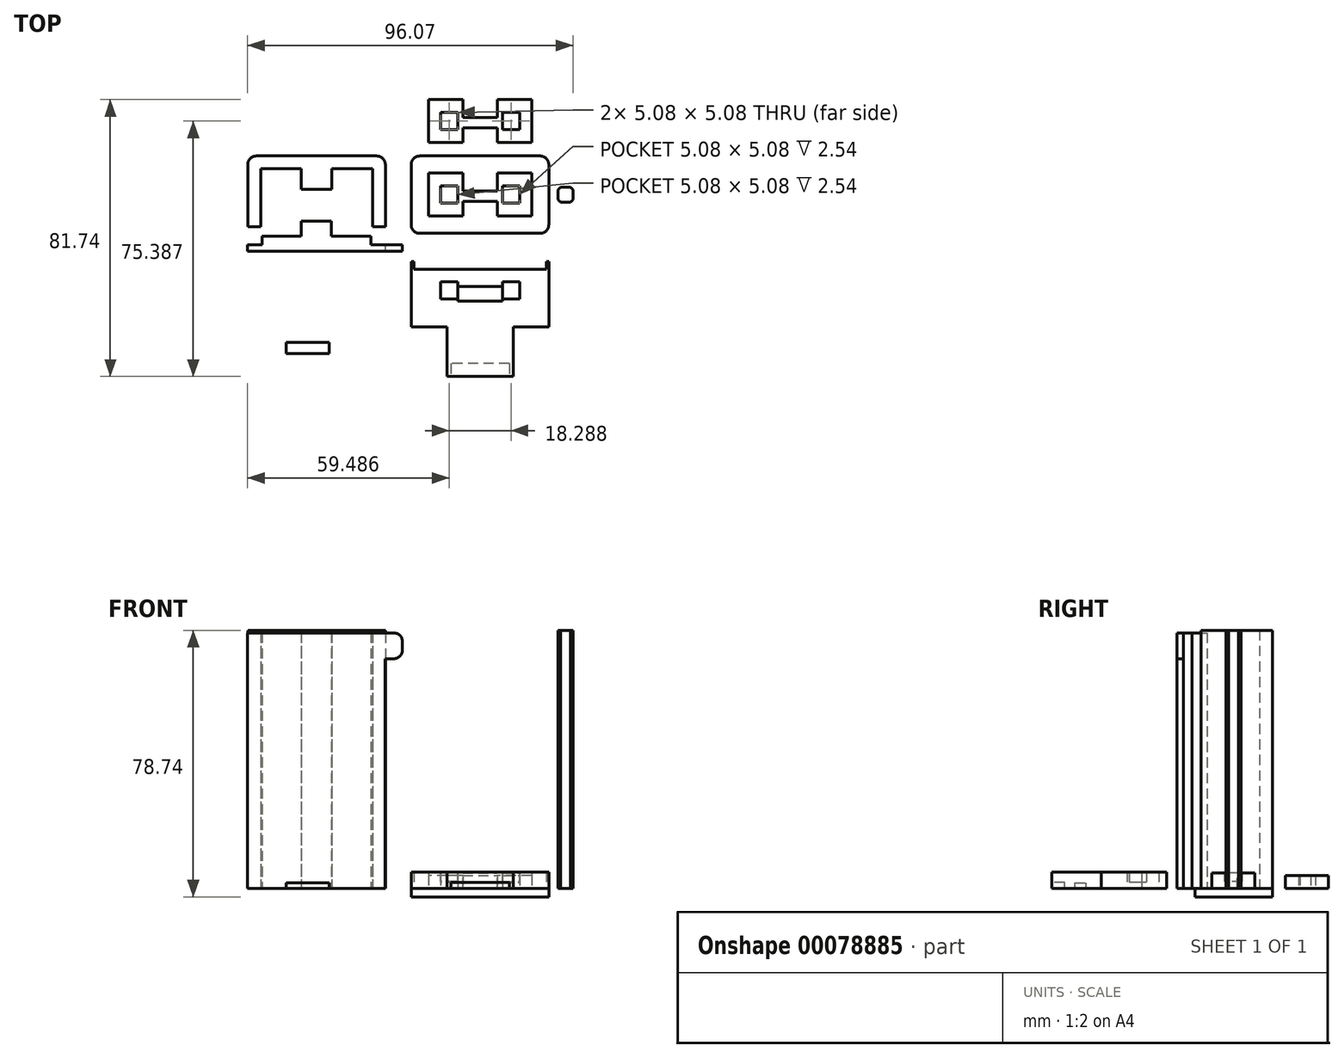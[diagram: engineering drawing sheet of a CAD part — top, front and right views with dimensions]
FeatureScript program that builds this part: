
annotation { "Feature Type Name" : "Feature", "Feature Type Description" : "" }
export const myFeature = defineFeature(function(context is Context, id is Id, definition is map)
    precondition{}
    {
        {
            var Q0;
            Q0=qCreatedBy(makeId("Top.planeOp"),FACE);
            var sketch = newSketch(context, id + "F0", { "sketchPlane" : qUnion([Q0])});
            skLineSegment(sketch, "E0.bottom", {"start": v(15.24, 6.35) * mm, "end": v(-15.24, 6.35) * mm});
            skLineSegment(sketch, "E0.top", {"start": v(15.24, -6.35) * mm, "end": v(-15.24, -6.35) * mm});
            skLineSegment(sketch, "E0.left", {"start": v(15.24, 6.35) * mm, "end": v(15.24, -6.35) * mm});
            skLineSegment(sketch, "E0.right", {"start": v(-15.24, 6.35) * mm, "end": v(-15.24, -6.35) * mm});
            skPoint(sketch, "E0.middle", {"position": v(0, 0) * mm});
            skSolve(sketch);
        }
        {
            var Q0;
            Q0=makeQuery(id+"F0.imprint","IMPRINT",FACE,{"disambiguationData":[TD([[makeQuery(id+"F0.imprint","IMPRINT",EDGE,{"derivedFrom":sQuery(id+"F0.wireOp",EDGE,"E0.bottom")}),1.0]])]});
            extrude(context, id + "F1", {"entities" : qUnion([Q0]), "depth" : 4.57 * mm});
        }
        {
            var Q0;
            Q0=makeQuery(id+"F1.opExtrude","CAP_FACE",FACE,{"disambiguationData":[OSD([sQuery(id+"F0.wireOp",EDGE,"E0.bottom"),sQuery(id+"F0.wireOp",EDGE,"E0.top"),sQuery(id+"F0.wireOp",EDGE,"E0.left"),sQuery(id+"F0.wireOp",EDGE,"E0.right")])],"isStart":false});
            var sketch = newSketch(context, id + "F2", { "sketchPlane" : qUnion([Q0])});
            skLineSegment(sketch, "E1", {"start": v(0, 6.35) * mm, "end": v(0, -2.03) * mm});
            skPoint(sketch, "E2", {"position": v(-15.24, 0) * mm});
            skLineSegment(sketch, "E3.bottom", {"start": v(-6.6, 2.54) * mm, "end": v(-11.68, 2.54) * mm});
            skLineSegment(sketch, "E3.top", {"start": v(-6.6, -2.54) * mm, "end": v(-11.68, -2.54) * mm});
            skLineSegment(sketch, "E3.left", {"start": v(-6.6, 2.54) * mm, "end": v(-6.6, -2.54) * mm});
            skLineSegment(sketch, "E3.right", {"start": v(-11.68, 2.54) * mm, "end": v(-11.68, -2.54) * mm});
            skPoint(sketch, "E3.middle", {"position": v(-9.14, 0) * mm});
            skLineSegment(sketch, "E4", {"start": v(-6.6, 2.54) * mm, "end": v(0, 2.54) * mm});
            skLineSegment(sketch, "E5.MirrorCS", {"start": v(11.68, 2.54) * mm, "end": v(11.68, -2.54) * mm});
            skLineSegment(sketch, "E6.MirrorCS", {"start": v(6.6, 2.54) * mm, "end": v(6.6, -2.54) * mm});
            skLineSegment(sketch, "E7.MirrorCS", {"start": v(6.6, 2.54) * mm, "end": v(11.68, 2.54) * mm});
            skLineSegment(sketch, "E8.MirrorCS", {"start": v(6.6, -2.54) * mm, "end": v(11.68, -2.54) * mm});
            skPoint(sketch, "E9.MirrorP", {"position": v(9.14, 0) * mm});
            skLineSegment(sketch, "E10", {"start": v(-5.08, 6.35) * mm, "end": v(-5.08, 1.02) * mm});
            skLineSegment(sketch, "E11", {"start": v(-5.08, 1.02) * mm, "end": v(0, 1.02) * mm});
            skLineSegment(sketch, "E12", {"start": v(0, 1.02) * mm, "end": v(5.08, 1.02) * mm});
            skLineSegment(sketch, "E13", {"start": v(5.08, 1.02) * mm, "end": v(5.08, 6.35) * mm});
            skPoint(sketch, "E14", {"position": v(0, 0) * mm});
            skLineSegment(sketch, "E15", {"start": v(0, 0) * mm, "end": v(-1.52, 0) * mm});
            skLineSegment(sketch, "E16.MirrorCS", {"start": v(-5.08, -6.6) * mm, "end": v(-5.08, -2.03) * mm});
            skLineSegment(sketch, "E17.MirrorCS", {"start": v(-5.08, -2.03) * mm, "end": v(0, -2.03) * mm});
            skLineSegment(sketch, "E18.MirrorCS", {"start": v(5.08, -2.03) * mm, "end": v(5.08, -6.6) * mm});
            skLineSegment(sketch, "E19.MirrorCS", {"start": v(0, -2.03) * mm, "end": v(5.08, -2.03) * mm});
            skLineSegment(sketch, "E20", {"start": v(0, -2.03) * mm, "end": v(0, -6.35) * mm});
            skSolve(sketch);
        }
        {
            var Q0;
            Q0=makeQuery(id+"F2.imprint","IMPRINT",FACE,{"disambiguationData":[TD([[makeQuery(id+"F2.imprint","IMPRINT",EDGE,{"derivedFrom":sQuery(id+"F2.wireOp",EDGE,"E3.bottom")}),1.0]])]});
            var Q1;
            Q1=makeQuery(id+"F2.imprint","IMPRINT",FACE,{"disambiguationData":[TD([[makeQuery(id+"F2.imprint","IMPRINT",EDGE,{"derivedFrom":sQuery(id+"F2.wireOp",EDGE,"E5.MirrorCS")}),-1.0]])]});
            extrude(context, id + "F3", {"entities" : qUnion([Q0, Q1]), "operationType" : NewBodyOperationType.REMOVE, "oppositeDirection" : true, "depth" : 2.54 * mm});
        }
        {
            var Q0;
            Q0 = qSketchRegion(id + "F5", true);
            var Q1;
            {var subQ3=sQuery(id+"F2.wireOp",EDGE,"E11");Q1=makeQuery(id+"F2.imprint","IMPRINT",FACE,{"disambiguationData":[TD([[makeQuery(id+"F2.imprint","IMPRINT",EDGE,{"derivedFrom":subQ3}),1.0]])]});}
            var Q2;
            {var subQ0=sQuery(id+"F2.wireOp",EDGE,"E1");var subQ1=makeQuery(id+"F1.opExtrude","CAP_EDGE",EDGE,{"disambiguationData":[OSD([sQuery(id+"F0.wireOp",EDGE,"E0.bottom")])],"isStart":false});var subQ2=makeQuery(id+"F2.imprint","INTERSECT",VERTEX,{"derivedFrom":[subQ1,subQ0]});Q2=makeQuery(id+"F2.imprint","IMPRINT",FACE,{"disambiguationData":[TD([[makeQuery(id+"F2.imprint","IMPRINT",EDGE,{"disambiguationData":[TD([[subQ2,-1.0]])],"derivedFrom":subQ0}),-1.0]])]});}
            var Q3;
            {var subQ0=sQuery(id+"F2.wireOp",EDGE,"E12");Q3=makeQuery(id+"F2.imprint","IMPRINT",FACE,{"disambiguationData":[TD([[makeQuery(id+"F2.imprint","IMPRINT",EDGE,{"derivedFrom":subQ0}),1.0]])]});}
            var Q4;
            {var subQ4=sQuery(id+"F2.wireOp",EDGE,"E18.MirrorCS");Q4=makeQuery(id+"F2.imprint","IMPRINT",FACE,{"disambiguationData":[TD([[makeQuery(id+"F2.imprint","IMPRINT",EDGE,{"derivedFrom":subQ4}),-1.0]])]});}
            var Q5;
            {var subQ4=sQuery(id+"F2.wireOp",EDGE,"E16.MirrorCS");Q5=makeQuery(id+"F2.imprint","IMPRINT",FACE,{"disambiguationData":[TD([[makeQuery(id+"F2.imprint","IMPRINT",EDGE,{"derivedFrom":subQ4}),-1.0]])]});}
            extrude(context, id + "F4", {"entities" : qUnion([Q0, Q1, Q2, Q3, Q4, Q5]), "operationType" : NewBodyOperationType.REMOVE, "oppositeDirection" : true, "depth" : 7.62 * mm});
        }
        {
            var Q0;
            Q0=makeQuery(id+"F1.opExtrude","CAP_FACE",FACE,{"disambiguationData":[OSD([sQuery(id+"F0.wireOp",EDGE,"E0.bottom"),sQuery(id+"F0.wireOp",EDGE,"E0.top"),sQuery(id+"F0.wireOp",EDGE,"E0.left"),sQuery(id+"F0.wireOp",EDGE,"E0.right")])],"isStart":true});
            var sketch = newSketch(context, id + "F5", { "sketchPlane" : qUnion([Q0])});
            skLineSegment(sketch, "E21.0", {"start": v(-20.32, -8.89) * mm, "end": v(-20.32, -6.82) * mm});
            skLineSegment(sketch, "E21.1", {"start": v(17.78, -11.43) * mm, "end": v(-17.28, -11.43) * mm});
            skLineSegment(sketch, "E21.2", {"start": v(20.32, -8.89) * mm, "end": v(20.32, 8.9) * mm});
            skLineSegment(sketch, "E21.3", {"start": v(17.78, 11.43) * mm, "end": v(-17.78, 11.43) * mm});
            skLineSegment(sketch, "E22", {"start": v(-20.32, -6.82) * mm, "end": v(-20.32, 8.9) * mm});
            skLineSegment(sketch, "E23", {"start": v(-17.28, -11.43) * mm, "end": v(-17.78, -11.43) * mm});
            skLineSegment(sketch, "E24.MirrorCS", {"start": v(-31.12, -10.16) * mm, "end": v(-31.12, -11.31) * mm});
            skLineSegment(sketch, "E25", {"start": v(20.32, 0) * mm, "end": v(18.07, 0) * mm});
            skPoint(sketch, "E25.endSnap0", {"position": v(20.32, 0) * mm});
            skLineSegment(sketch, "E26", {"start": v(0, 11.43) * mm, "end": v(0, 9.36) * mm});
            skPoint(sketch, "E26.endSnap0", {"position": v(0, 11.43) * mm});
            skPoint(sketch, "E27.visualSharp", {"position": v(-20.32, -11.43) * mm});
            skArc(sketch, "E27.filletArc", {"start": v(-20.32, -8.9) * mm, "mid": v(-19.58, -10.69) * mm, "end": v(-17.78, -11.43) * mm});
            skPoint(sketch, "E28.visualSharp", {"position": v(-20.32, 11.43) * mm});
            skArc(sketch, "E28.filletArc", {"start": v(-17.78, 11.43) * mm, "mid": v(-19.58, 10.69) * mm, "end": v(-20.32, 8.9) * mm});
            skPoint(sketch, "E29.visualSharp", {"position": v(20.32, 11.43) * mm});
            skArc(sketch, "E29.filletArc", {"start": v(20.32, 8.9) * mm, "mid": v(19.58, 10.69) * mm, "end": v(17.78, 11.43) * mm});
            skPoint(sketch, "E30.visualSharp", {"position": v(20.32, -11.43) * mm});
            skArc(sketch, "E30.filletArc", {"start": v(17.78, -11.43) * mm, "mid": v(19.58, -10.69) * mm, "end": v(20.32, -8.89) * mm});
            skSolve(sketch);
        }
        {
            var Q0;
            Q0=makeQuery(id+"F5.imprint","IMPRINT",FACE,{"disambiguationData":[TD([[makeQuery(id+"F5.imprint","IMPRINT",EDGE,{"derivedFrom":sQuery(id+"F5.wireOp",EDGE,"E21.0")}),-1.0]])]});
            var Q1;
            {var subQ1=sQuery(id+"F0.wireOp",EDGE,"E0.left");Q1=makeQuery(id+"F5.imprint","IMPRINT",FACE,{"disambiguationData":[TD([[makeQuery(id+"F5.imprint","IMPRINT",EDGE,{"derivedFrom":makeQuery(id+"F1.opExtrude","CAP_EDGE",EDGE,{"disambiguationData":[OSD([subQ1])],"isStart":true})}),1.0]])]});}
            extrude(context, id + "F6", {"entities" : qUnion([Q0, Q1]), "operationType" : NewBodyOperationType.ADD, "depth" : 2.54 * mm});
        }
        {
            var Q0;
            Q0=qCreatedBy(makeId("Top.planeOp"),FACE);
            var sketch = newSketch(context, id + "F7", { "sketchPlane" : qUnion([Q0])});
            skLineSegment(sketch, "E31.bottom", {"start": v(27.44, 2.22) * mm, "end": v(23.76, 2.22) * mm});
            skLineSegment(sketch, "E31.top", {"start": v(27.44, -2.22) * mm, "end": v(23, -2.22) * mm});
            skLineSegment(sketch, "E31.left", {"start": v(27.44, 2.22) * mm, "end": v(27.44, -2.22) * mm});
            skLineSegment(sketch, "E31.right", {"start": v(23, 2.22) * mm, "end": v(23, 1.46) * mm});
            skPoint(sketch, "E31.middle", {"position": v(25.22, 0) * mm});
            skLineSegment(sketch, "E32", {"start": v(23, 1.46) * mm, "end": v(23, -2.22) * mm});
            skLineSegment(sketch, "E33", {"start": v(23.76, 2.22) * mm, "end": v(23, 2.22) * mm});
            skLineSegment(sketch, "E34", {"start": v(23, 1.46) * mm, "end": v(23.76, 2.22) * mm});
            skLineSegment(sketch, "E35", {"start": v(25.22, -2.22) * mm, "end": v(25.22, -1.41) * mm});
            skLineSegment(sketch, "E36", {"start": v(27.44, 0) * mm, "end": v(27, 0) * mm});
            skPoint(sketch, "E36.endSnap0", {"position": v(27.44, 0) * mm});
            skLineSegment(sketch, "E37.MirrorCS", {"start": v(27.44, 1.46) * mm, "end": v(26.68, 2.22) * mm});
            skLineSegment(sketch, "E38.MirrorCS", {"start": v(27.44, -1.46) * mm, "end": v(26.68, -2.22) * mm});
            skLineSegment(sketch, "E39.MirrorCS", {"start": v(23, -1.46) * mm, "end": v(23.76, -2.22) * mm});
            skSolve(sketch);
        }
        {
            var Q0;
            {var subQ7=sQuery(id+"F7.wireOp",EDGE,"E34");Q0=makeQuery(id+"F7.imprint","IMPRINT",FACE,{"disambiguationData":[TD([[makeQuery(id+"F7.imprint","IMPRINT",EDGE,{"derivedFrom":subQ7}),-1.0]])]});}
            extrude(context, id + "F8", {"entities" : qUnion([Q0]), "depth" : 76.2 * mm});
        }
        {
            var Q0;
            Q0=qCreatedBy(makeId("Top.planeOp"),FACE);
            var sketch = newSketch(context, id + "F9", { "sketchPlane" : qUnion([Q0])});
            skLineSegment(sketch, "E40.bottom", {"start": v(15.24, 28.07) * mm, "end": v(-15.24, 28.07) * mm});
            skLineSegment(sketch, "E40.top", {"start": v(15.24, 15.37) * mm, "end": v(-15.24, 15.37) * mm});
            skLineSegment(sketch, "E40.left", {"start": v(15.24, 28.07) * mm, "end": v(15.24, 15.37) * mm});
            skLineSegment(sketch, "E40.right", {"start": v(-15.24, 28.07) * mm, "end": v(-15.24, 15.37) * mm});
            skPoint(sketch, "E40.middle", {"position": v(0, 21.72) * mm});
            skLineSegment(sketch, "E41.bottom", {"start": v(-6.6, 24.26) * mm, "end": v(-11.68, 24.26) * mm});
            skLineSegment(sketch, "E41.top", {"start": v(-6.6, 19.18) * mm, "end": v(-11.68, 19.18) * mm});
            skLineSegment(sketch, "E41.left", {"start": v(-6.6, 24.26) * mm, "end": v(-6.6, 19.18) * mm});
            skLineSegment(sketch, "E41.right", {"start": v(-11.68, 24.26) * mm, "end": v(-11.68, 19.18) * mm});
            skPoint(sketch, "E41.middle", {"position": v(-9.14, 21.72) * mm});
            skLineSegment(sketch, "E42", {"start": v(0, 21.72) * mm, "end": v(0, 28.07) * mm});
            skPoint(sketch, "E43", {"position": v(-15.24, 21.72) * mm});
            skLineSegment(sketch, "E44", {"start": v(-6.6, 24.26) * mm, "end": v(0, 24.26) * mm});
            skPoint(sketch, "E45.MirrorP", {"position": v(9.14, 21.72) * mm});
            skLineSegment(sketch, "E46.MirrorCS", {"start": v(11.68, 24.26) * mm, "end": v(11.68, 19.18) * mm});
            skLineSegment(sketch, "E47.MirrorCS", {"start": v(6.6, 24.26) * mm, "end": v(6.6, 19.18) * mm});
            skLineSegment(sketch, "E48.MirrorCS", {"start": v(6.6, 24.26) * mm, "end": v(11.68, 24.26) * mm});
            skLineSegment(sketch, "E49.MirrorCS", {"start": v(6.6, 19.18) * mm, "end": v(11.68, 19.18) * mm});
            skLineSegment(sketch, "E50", {"start": v(-5.08, 28.07) * mm, "end": v(-5.08, 22.73) * mm});
            skLineSegment(sketch, "E51", {"start": v(-5.08, 22.73) * mm, "end": v(0, 22.73) * mm});
            skLineSegment(sketch, "E52", {"start": v(0, 22.73) * mm, "end": v(5.08, 22.73) * mm});
            skLineSegment(sketch, "E53", {"start": v(5.08, 22.73) * mm, "end": v(5.08, 28.07) * mm});
            skLineSegment(sketch, "E54", {"start": v(0, 21.72) * mm, "end": v(-2.4, 21.72) * mm});
            skLineSegment(sketch, "E55.MirrorCS", {"start": v(-5.08, 15.11) * mm, "end": v(-5.08, 19.68) * mm});
            skLineSegment(sketch, "E56.MirrorCS", {"start": v(-5.08, 19.68) * mm, "end": v(0, 19.68) * mm});
            skLineSegment(sketch, "E57.MirrorCS", {"start": v(5.08, 19.68) * mm, "end": v(5.08, 15.37) * mm});
            skLineSegment(sketch, "E58.MirrorCS", {"start": v(0, 19.68) * mm, "end": v(5.08, 19.68) * mm});
            skSolve(sketch);
        }
        {
            var Q0;
            Q0=makeQuery(id+"F9.imprint","IMPRINT",FACE,{"disambiguationData":[TD([[makeQuery(id+"F9.imprint","IMPRINT",EDGE,{"derivedFrom":sQuery(id+"F9.wireOp",EDGE,"E40.top")}),-1.0]])]});
            extrude(context, id + "F10", {"entities" : qUnion([Q0]), "depth" : 3.8 * mm});
        }
        {
            var Q0;
            Q0=qCreatedBy(makeId("Top.planeOp"),FACE);
            var sketch = newSketch(context, id + "F11", { "sketchPlane" : qUnion([Q0])});
            skLineSegment(sketch, "E59.bottom", {"start": v(-31.76, 7.62) * mm, "end": v(-64.78, 7.62) * mm});
            skLineSegment(sketch, "E59.top", {"start": v(-31.76, -7.62) * mm, "end": v(-64.78, -7.62) * mm});
            skLineSegment(sketch, "E59.left", {"start": v(-31.76, 7.62) * mm, "end": v(-31.76, -7.62) * mm});
            skLineSegment(sketch, "E59.right", {"start": v(-64.78, 7.62) * mm, "end": v(-64.78, -7.62) * mm});
            skPoint(sketch, "E59.middle", {"position": v(-48.27, 0) * mm});
            skLineSegment(sketch, "E60.0", {"start": v(-30.49, 11.43) * mm, "end": v(-66.05, 11.43) * mm});
            skLineSegment(sketch, "E60.1", {"start": v(-27.95, 8.9) * mm, "end": v(-27.95, -9.53) * mm});
            skLineSegment(sketch, "E60.2", {"start": v(-27.95, -11.43) * mm, "end": v(-68.59, -11.43) * mm});
            skLineSegment(sketch, "E60.3", {"start": v(-68.59, 8.89) * mm, "end": v(-68.59, -9.53) * mm});
            skLineSegment(sketch, "E61", {"start": v(-64.78, -7.62) * mm, "end": v(-64.78, -11.43) * mm});
            skLineSegment(sketch, "E62", {"start": v(-31.76, -7.62) * mm, "end": v(-31.76, -11.43) * mm});
            skPoint(sketch, "E63", {"position": v(-48.27, 11.43) * mm});
            skLineSegment(sketch, "E64", {"start": v(-52.71, 7.62) * mm, "end": v(-52.71, 1.52) * mm});
            skLineSegment(sketch, "E65", {"start": v(-52.71, 1.52) * mm, "end": v(-43.82, 1.52) * mm});
            skLineSegment(sketch, "E66", {"start": v(-43.82, 1.52) * mm, "end": v(-43.82, 7.62) * mm});
            skPoint(sketch, "E67", {"position": v(-48.27, 1.52) * mm});
            skLineSegment(sketch, "E68", {"start": v(-27.95, -9.53) * mm, "end": v(-31.76, -9.53) * mm});
            skLineSegment(sketch, "E69", {"start": v(-27.95, -9.53) * mm, "end": v(-27.95, -11.43) * mm});
            skLineSegment(sketch, "E70", {"start": v(-64.78, -9.53) * mm, "end": v(-68.59, -9.53) * mm});
            skLineSegment(sketch, "E71", {"start": v(-68.59, -9.53) * mm, "end": v(-68.59, -11.43) * mm});
            skPoint(sketch, "E72.visualSharp", {"position": v(-27.95, 11.43) * mm});
            skArc(sketch, "E72.filletArc", {"start": v(-27.95, 8.9) * mm, "mid": v(-28.69, 10.69) * mm, "end": v(-30.49, 11.43) * mm});
            skPoint(sketch, "E73.visualSharp", {"position": v(-68.59, 11.43) * mm});
            skArc(sketch, "E73.filletArc", {"start": v(-66.05, 11.43) * mm, "mid": v(-67.84, 10.69) * mm, "end": v(-68.59, 8.89) * mm});
            skSolve(sketch);
        }
        {
            var Q0;
            {var subQ0=sQuery(id+"F11.wireOp",EDGE,"E64");Q0=makeQuery(id+"F11.imprint","IMPRINT",FACE,{"disambiguationData":[TD([[makeQuery(id+"F11.imprint","IMPRINT",EDGE,{"derivedFrom":subQ0}),1.0]])]});}
            var Q1;
            {var subQ5=sQuery(id+"F11.wireOp",EDGE,"E59.left");Q1=makeQuery(id+"F11.imprint","IMPRINT",FACE,{"disambiguationData":[TD([[makeQuery(id+"F11.imprint","IMPRINT",EDGE,{"derivedFrom":subQ5}),1.0]])]});}
            extrude(context, id + "F12", {"entities" : qUnion([Q0, Q1]), "depth" : 76.2 * mm});
        }
        {
            var Q0;
            Q0=qCreatedBy(makeId("Top.planeOp"),FACE);
            var sketch = newSketch(context, id + "F13", { "sketchPlane" : qUnion([Q0])});
            skLineSegment(sketch, "E74.bottom", {"start": v(20.32, -17.47) * mm, "end": v(-20.32, -17.47) * mm});
            skLineSegment(sketch, "E74.top", {"start": v(20.32, -39.06) * mm, "end": v(-20.32, -39.06) * mm});
            skLineSegment(sketch, "E74.left", {"start": v(20.32, -17.47) * mm, "end": v(20.32, -39.06) * mm});
            skLineSegment(sketch, "E74.right", {"start": v(-20.32, -17.47) * mm, "end": v(-20.32, -39.06) * mm});
            skPoint(sketch, "E74.middle", {"position": v(0, -28.27) * mm});
            skLineSegment(sketch, "E75.bottom", {"start": v(-6.6, -25.73) * mm, "end": v(-11.68, -25.73) * mm});
            skLineSegment(sketch, "E75.top", {"start": v(-6.6, -30.8) * mm, "end": v(-11.68, -30.8) * mm});
            skLineSegment(sketch, "E75.left", {"start": v(-6.6, -25.73) * mm, "end": v(-6.6, -30.8) * mm});
            skLineSegment(sketch, "E75.right", {"start": v(-11.68, -25.73) * mm, "end": v(-11.68, -30.8) * mm});
            skPoint(sketch, "E75.middle", {"position": v(-9.14, -28.27) * mm});
            skLineSegment(sketch, "E76", {"start": v(0, -28.27) * mm, "end": v(0, -39.06) * mm});
            skLineSegment(sketch, "E77", {"start": v(0, -28.27) * mm, "end": v(-6.6, -28.27) * mm});
            skLineSegment(sketch, "E78.MirrorCS", {"start": v(6.6, -30.8) * mm, "end": v(11.68, -30.8) * mm});
            skLineSegment(sketch, "E79.MirrorCS", {"start": v(6.6, -25.73) * mm, "end": v(11.68, -25.73) * mm});
            skLineSegment(sketch, "E80.MirrorCS", {"start": v(11.68, -25.73) * mm, "end": v(11.68, -30.8) * mm});
            skLineSegment(sketch, "E81.MirrorCS", {"start": v(6.6, -25.73) * mm, "end": v(6.6, -30.8) * mm});
            skPoint(sketch, "E82.MirrorP", {"position": v(9.14, -28.27) * mm});
            skLineSegment(sketch, "E83", {"start": v(-19.56, -17.47) * mm, "end": v(-19.56, -22.05) * mm});
            skLineSegment(sketch, "E84", {"start": v(-19.56, -22.05) * mm, "end": v(19.56, -22.05) * mm});
            skLineSegment(sketch, "E85", {"start": v(19.56, -22.05) * mm, "end": v(19.56, -17.47) * mm});
            skPoint(sketch, "E86", {"position": v(0, -22.05) * mm});
            skLineSegment(sketch, "E87", {"start": v(0, -22.05) * mm, "end": v(0, -27.13) * mm});
            skLineSegment(sketch, "E88", {"start": v(0, -27.13) * mm, "end": v(-6.6, -27.13) * mm});
            skLineSegment(sketch, "E89", {"start": v(0, -27.13) * mm, "end": v(6.6, -27.13) * mm});
            skLineSegment(sketch, "E90", {"start": v(6.6, -30.8) * mm, "end": v(6.6, -31.44) * mm});
            skLineSegment(sketch, "E91", {"start": v(6.6, -31.44) * mm, "end": v(-6.6, -31.44) * mm});
            skLineSegment(sketch, "E92", {"start": v(-6.6, -31.44) * mm, "end": v(-6.6, -30.8) * mm});
            skLineSegment(sketch, "E93.top", {"start": v(20.32, -53.67) * mm, "end": v(9.78, -53.67) * mm});
            skLineSegment(sketch, "E93.left", {"start": v(20.32, -39.06) * mm, "end": v(20.32, -53.67) * mm});
            skLineSegment(sketch, "E93.right", {"start": v(-20.32, -39.06) * mm, "end": v(-20.32, -53.67) * mm});
            skLineSegment(sketch, "E94", {"start": v(-9.78, -53.67) * mm, "end": v(-20.32, -53.67) * mm});
            skLineSegment(sketch, "E95", {"start": v(9.78, -53.67) * mm, "end": v(-9.78, -53.67) * mm});
            skLineSegment(sketch, "E96", {"start": v(-9.78, -53.67) * mm, "end": v(-9.78, -39.06) * mm});
            skLineSegment(sketch, "E97", {"start": v(9.78, -53.67) * mm, "end": v(9.78, -39.06) * mm});
            skPoint(sketch, "E98", {"position": v(0, -53.67) * mm});
            skLineSegment(sketch, "E99", {"start": v(19.56, -19.76) * mm, "end": v(20.32, -19.76) * mm});
            skLineSegment(sketch, "E100.MirrorCS", {"start": v(0, -17.47) * mm, "end": v(0, -12.4) * mm});
            skLineSegment(sketch, "E101.MirrorCS", {"start": v(-19.56, -19.76) * mm, "end": v(-20.32, -19.76) * mm});
            skSolve(sketch);
        }
        {
            var Q0;
            Q0=makeQuery(id+"F13.imprint","IMPRINT",FACE,{"disambiguationData":[TD([[makeQuery(id+"F13.imprint","IMPRINT",EDGE,{"derivedFrom":sQuery(id+"F13.wireOp",EDGE,"E95")}),-1.0]])]});
            var Q1;
            {var subQ15=sQuery(id+"F13.wireOp",EDGE,"E75.bottom");Q1=makeQuery(id+"F13.imprint","IMPRINT",FACE,{"disambiguationData":[TD([[makeQuery(id+"F13.imprint","IMPRINT",EDGE,{"derivedFrom":subQ15}),-1.0]])]});}
            var Q2;
            Q2=makeQuery(id+"F13.imprint","IMPRINT",FACE,{"disambiguationData":[TD([[makeQuery(id+"F13.imprint","IMPRINT",EDGE,{"derivedFrom":sQuery(id+"F13.wireOp",EDGE,"E78.MirrorCS")}),-1.0]])]});
            extrude(context, id + "F14", {"entities" : qUnion([Q0, Q1, Q2]), "depth" : 4.83 * mm});
        }
        {
            var Q0;
            {var subQ3=sQuery(id+"F13.wireOp",EDGE,"E75.bottom");Q0=makeQuery(id+"F13.imprint","IMPRINT",FACE,{"disambiguationData":[TD([[makeQuery(id+"F13.imprint","IMPRINT",EDGE,{"derivedFrom":subQ3}),1.0]])]});}
            var Q1;
            Q1=makeQuery(id+"F13.imprint","IMPRINT",FACE,{"disambiguationData":[TD([[makeQuery(id+"F13.imprint","IMPRINT",EDGE,{"derivedFrom":sQuery(id+"F13.wireOp",EDGE,"E78.MirrorCS")}),1.0]])]});
            extrude(context, id + "F15", {"entities" : qUnion([Q0, Q1]), "operationType" : NewBodyOperationType.ADD, "depth" : 1.78 * mm});
        }
        {
            var Q0;
            Q0=makeQuery(id+"F14.opExtrude","SWEPT_FACE",FACE,{"disambiguationData":[OSD([sQuery(id+"F13.wireOp",EDGE,"E95")])]});
            var sketch = newSketch(context, id + "F16", { "sketchPlane" : qUnion([Q0])});
            skLineSegment(sketch, "E102.bottom", {"start": v(-8.64, 4.83) * mm, "end": v(8.64, 4.83) * mm});
            skLineSegment(sketch, "E102.top", {"start": v(-8.64, 3.05) * mm, "end": v(8.64, 3.05) * mm});
            skLineSegment(sketch, "E102.left", {"start": v(-8.64, 4.83) * mm, "end": v(-8.64, 3.05) * mm});
            skLineSegment(sketch, "E102.right", {"start": v(8.64, 4.83) * mm, "end": v(8.64, 3.05) * mm});
            skPoint(sketch, "E103", {"position": v(0, 3.05) * mm});
            skPoint(sketch, "E104", {"position": v(-9.78, 2.41) * mm});
            skLineSegment(sketch, "E105", {"start": v(-9.78, 2.41) * mm, "end": v(-7.47, 2.41) * mm});
            skLineSegment(sketch, "E106.MirrorCS", {"start": v(8.64, 0) * mm, "end": v(8.64, 1.78) * mm});
            skLineSegment(sketch, "E107.MirrorCS", {"start": v(-8.64, 0) * mm, "end": v(-8.64, 1.78) * mm});
            skLineSegment(sketch, "E108.MirrorCS", {"start": v(-8.64, 1.78) * mm, "end": v(8.64, 1.78) * mm});
            skSolve(sketch);
        }
        {
            var Q0;
            {var subQ0=sQuery(id+"F16.wireOp",EDGE,"E106.MirrorCS");Q0=makeQuery(id+"F16.imprint","IMPRINT",FACE,{"disambiguationData":[TD([[makeQuery(id+"F16.imprint","IMPRINT",EDGE,{"derivedFrom":subQ0}),1.0]])]});}
            extrude(context, id + "F17", {"entities" : qUnion([Q0]), "operationType" : NewBodyOperationType.REMOVE, "oppositeDirection" : true, "depth" : 3.8 * mm});
        }
        {
            var Q0;
            Q0=qCreatedBy(makeId("Top.planeOp"),FACE);
            var sketch = newSketch(context, id + "F18", { "sketchPlane" : qUnion([Q0])});
            skLineSegment(sketch, "E109.bottom", {"start": v(-44.5, -46.91) * mm, "end": v(-57.2, -46.91) * mm});
            skLineSegment(sketch, "E109.top", {"start": v(-44.5, -43.61) * mm, "end": v(-57.2, -43.61) * mm});
            skLineSegment(sketch, "E109.left", {"start": v(-44.5, -46.91) * mm, "end": v(-44.5, -43.61) * mm});
            skLineSegment(sketch, "E109.right", {"start": v(-57.2, -46.91) * mm, "end": v(-57.2, -43.61) * mm});
            skPoint(sketch, "E109.middle", {"position": v(-50.86, -45.26) * mm});
            skSolve(sketch);
        }
        {
            var Q0;
            Q0=makeQuery(id+"F18.imprint","IMPRINT",FACE,{"disambiguationData":[TD([[makeQuery(id+"F18.imprint","IMPRINT",EDGE,{"derivedFrom":sQuery(id+"F18.wireOp",EDGE,"E109.bottom")}),-1.0]])]});
            extrude(context, id + "F19", {"entities" : qUnion([Q0]), "depth" : 1.59 * mm});
        }
        {
            var Q0;
            Q0=qCreatedBy(makeId("Top.planeOp"),FACE);
            var sketch = newSketch(context, id + "F20", { "sketchPlane" : qUnion([Q0])});
            skLineSegment(sketch, "E110.bottom", {"start": v(-28, -16.7) * mm, "end": v(-68.63, -16.7) * mm});
            skLineSegment(sketch, "E110.top", {"start": v(-28, -14.8) * mm, "end": v(-32.25, -14.8) * mm});
            skLineSegment(sketch, "E110.left", {"start": v(-28, -16.7) * mm, "end": v(-28, -14.8) * mm});
            skLineSegment(sketch, "E110.right", {"start": v(-68.63, -16.7) * mm, "end": v(-68.63, -14.8) * mm});
            skLineSegment(sketch, "E111.bottom", {"start": v(-32.25, -14.8) * mm, "end": v(-64.38, -14.8) * mm});
            skLineSegment(sketch, "E111.top", {"start": v(-32.25, -12.26) * mm, "end": v(-43.87, -12.26) * mm});
            skLineSegment(sketch, "E111.left", {"start": v(-32.25, -14.8) * mm, "end": v(-32.25, -14.8) * mm});
            skLineSegment(sketch, "E111.right", {"start": v(-64.38, -14.8) * mm, "end": v(-64.38, -12.26) * mm});
            skLineSegment(sketch, "E112", {"start": v(-32.25, -14.8) * mm, "end": v(-32.25, -12.26) * mm});
            skLineSegment(sketch, "E113", {"start": v(-64.38, -14.8) * mm, "end": v(-64.38, -14.8) * mm});
            skLineSegment(sketch, "E114", {"start": v(-64.38, -14.8) * mm, "end": v(-68.63, -14.8) * mm});
            skLineSegment(sketch, "E115.bottom", {"start": v(-43.87, -12.26) * mm, "end": v(-52.76, -12.26) * mm});
            skLineSegment(sketch, "E115.top", {"start": v(-43.87, -7.81) * mm, "end": v(-52.76, -7.81) * mm});
            skLineSegment(sketch, "E115.left", {"start": v(-43.87, -12.26) * mm, "end": v(-43.87, -7.81) * mm});
            skLineSegment(sketch, "E115.right", {"start": v(-52.76, -12.26) * mm, "end": v(-52.76, -7.81) * mm});
            skLineSegment(sketch, "E116", {"start": v(-52.76, -12.26) * mm, "end": v(-64.38, -12.26) * mm});
            skSolve(sketch);
        }
        {
            var Q0;
            Q0=makeQuery(id+"F20.imprint","IMPRINT",FACE,{"disambiguationData":[TD([[makeQuery(id+"F20.imprint","IMPRINT",EDGE,{"derivedFrom":sQuery(id+"F20.wireOp",EDGE,"E115.top")}),1.0]])]});
            var Q1;
            Q1=makeQuery(id+"F20.imprint","IMPRINT",FACE,{"disambiguationData":[TD([[makeQuery(id+"F20.imprint","IMPRINT",EDGE,{"derivedFrom":sQuery(id+"F20.wireOp",EDGE,"E111.top")}),1.0]])]});
            var Q2;
            Q2=makeQuery(id+"F20.imprint","IMPRINT",FACE,{"disambiguationData":[TD([[makeQuery(id+"F20.imprint","IMPRINT",EDGE,{"derivedFrom":sQuery(id+"F20.wireOp",EDGE,"E110.bottom")}),-1.0]])]});
            extrude(context, id + "F21", {"entities" : qUnion([Q0, Q1, Q2]), "depth" : 75.44 * mm});
        }
        {
            var Q0;
            Q0=makeQuery(id+"F21.opExtrude","SWEPT_FACE",FACE,{"disambiguationData":[OSD([sQuery(id+"F20.wireOp",EDGE,"E110.left")])]});
            var sketch = newSketch(context, id + "F22", { "sketchPlane" : qUnion([Q0])});
            skLineSegment(sketch, "E117.bottom", {"start": v(-14.8, 75.44) * mm, "end": v(-16.7, 75.44) * mm});
            skLineSegment(sketch, "E117.top", {"start": v(-14.8, 67.82) * mm, "end": v(-16.7, 67.82) * mm});
            skLineSegment(sketch, "E117.left", {"start": v(-14.8, 75.44) * mm, "end": v(-14.8, 67.82) * mm});
            skLineSegment(sketch, "E117.right", {"start": v(-16.7, 75.44) * mm, "end": v(-16.7, 67.82) * mm});
            skSolve(sketch);
        }
        {
            var Q0;
            Q0=makeQuery(id+"F22.imprint","IMPRINT",FACE,{"disambiguationData":[TD([[makeQuery(id+"F22.imprint","IMPRINT",EDGE,{"derivedFrom":sQuery(id+"F22.wireOp",EDGE,"E117.bottom")}),-1.0]])]});
            extrude(context, id + "F23", {"entities" : qUnion([Q0]), "operationType" : NewBodyOperationType.ADD, "depth" : 5.08 * mm});
        }
        {
            var Q0;
            Q0=makeQuery(id+"F23.opExtrude","CAP_EDGE",EDGE,{"disambiguationData":[OSD([sQuery(id+"F22.wireOp",EDGE,"E117.bottom")])],"isStart":false});
            fillet(context, id + "F24", {"entities" : qUnion([Q0]), "radius" : 2.54 * mm, "tangentPropagation" : true, "allowEdgeOverflow" : false});
        }
        {
            var Q0;
            Q0=makeQuery(id+"F23.opExtrude","CAP_EDGE",EDGE,{"disambiguationData":[OSD([sQuery(id+"F22.wireOp",EDGE,"E117.top")])],"isStart":false});
            fillet(context, id + "F25", {"entities" : qUnion([Q0]), "radius" : 2.54 * mm, "tangentPropagation" : true, "allowEdgeOverflow" : false});
        }
    });
